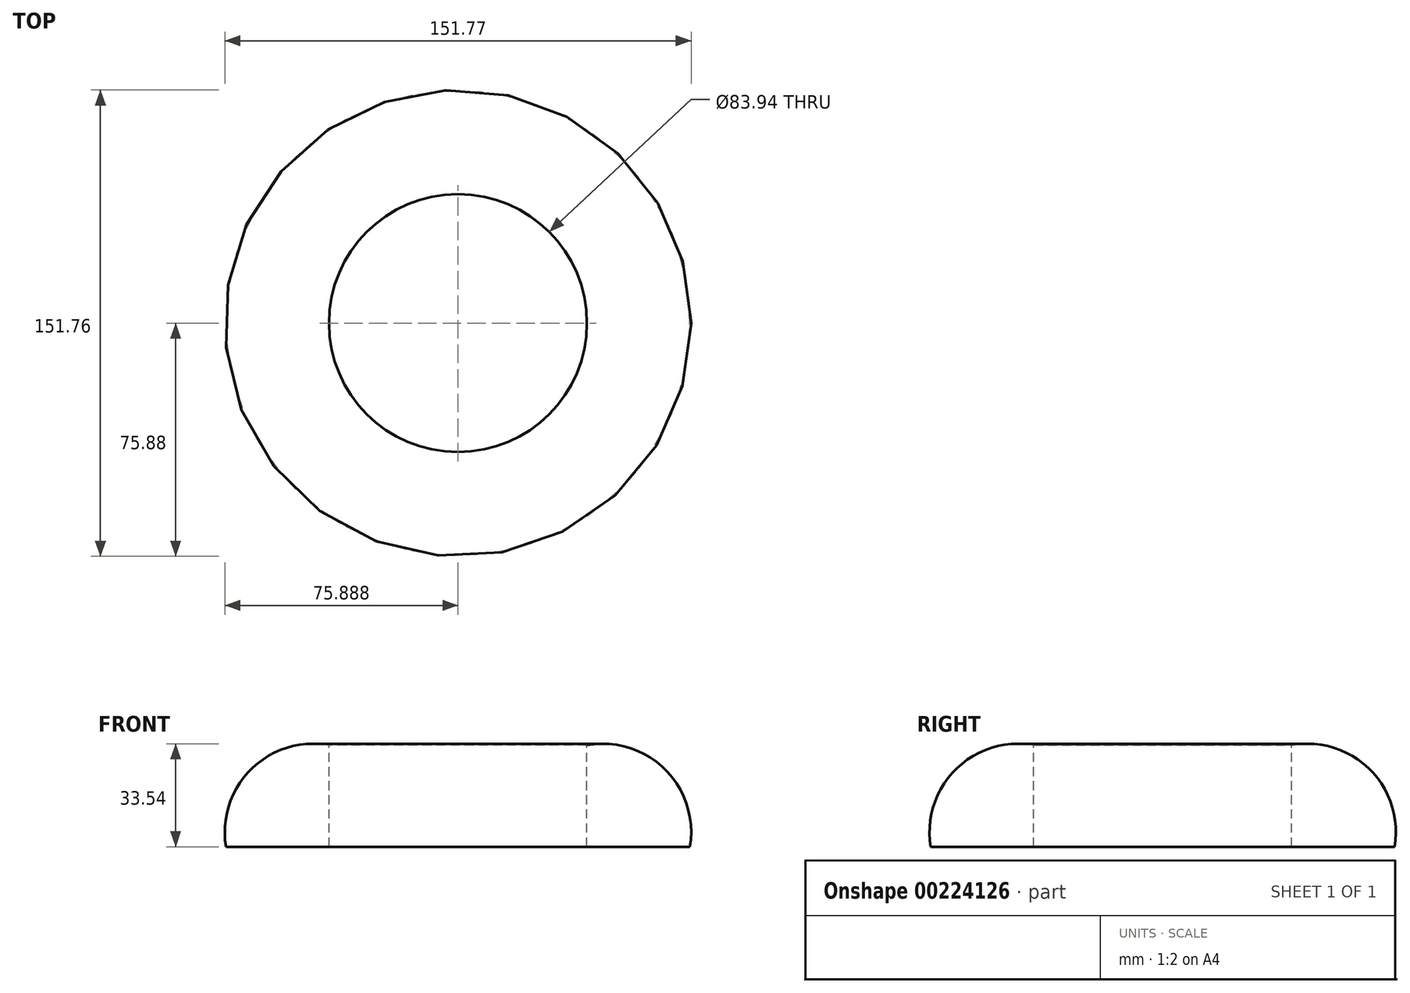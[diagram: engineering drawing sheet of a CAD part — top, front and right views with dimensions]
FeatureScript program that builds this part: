
annotation { "Feature Type Name" : "Feature", "Feature Type Description" : "" }
export const myFeature = defineFeature(function(context is Context, id is Id, definition is map)
    precondition{}
    {
        {
            var Q0;
            Q0=qCreatedBy(makeId("Front.planeOp"),FACE);
            var sketch = newSketch(context, id + "F0", { "sketchPlane" : qUnion([Q0])});
            skLineSegment(sketch, "E0", {"start": v(0, 33.08) * mm, "end": v(0, 0) * mm});
            skLineSegment(sketch, "E1", {"start": v(0, 0) * mm, "end": v(33.52, 0) * mm});
            skArc(sketch, "E2", {"start": v(33.52, 0) * mm, "mid": v(25.34, 25.24) * mm, "end": v(0, 33.08) * mm});
            skLineSegment(sketch, "E3", {"start": v(-41.97, 28.71) * mm, "end": v(-41.97, -33.67) * mm});
            skSolve(sketch);
        }
        {
            var Q0;
            Q0=makeQuery(id+"F0.imprint","IMPRINT",FACE,{"disambiguationData":[TD([[makeQuery(id+"F0.imprint","IMPRINT",EDGE,{"derivedFrom":sQuery(id+"F0.wireOp",EDGE,"E0")}),1.0]])]});
            var Q1;
            Q1=sQuery(id+"F0.wireOp",EDGE,"E3");
            revolve(context, id + "F1", {"entities" : qUnion([Q0]), "axis" : qUnion([Q1]), "revolveType" : RevolveType.FULL});
        }
    });
